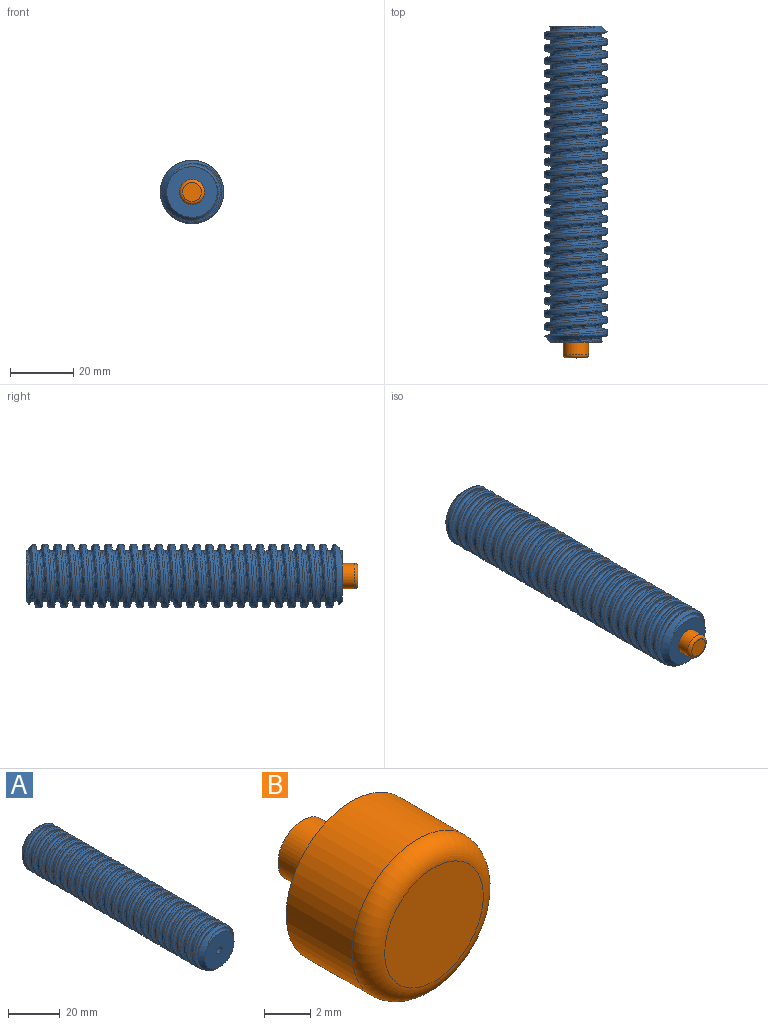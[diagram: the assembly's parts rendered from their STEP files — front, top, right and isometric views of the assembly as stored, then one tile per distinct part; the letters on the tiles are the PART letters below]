
ASSEMBLY  parts=2 mates=1
PART A: 13 faces, bbox 20x102.1x23.1 mm
  f0: cylinder r=10mm len=96mm, axis (0,1,0), area 2402.1mm2, adj f3,f4,f11,f12
  f1: plane 16x16mm, normal (0,-1,0), area 194mm2, adj f4,f7
  f2: plane 16x16mm, normal (0,1,0), area 201.1mm2, adj f3,f9
  f3: cone r=10mm half-angle=45deg, axis (0,-1,0), area 91.7mm2, adj f0,f2,f5,f6,f9,f10,f11,f12
  f4: cone r=8mm half-angle=45deg, axis (0,1,0), area 91.7mm2, adj f0,f1,f5,f6,f9,f10,f11,f12
  f5: bspline ~98.67x23.09mm, area 709.7mm2, adj f3,f4,f9,f12
  f6: bspline ~98.67x23.09mm, area 711.5mm2, adj f3,f4,f10,f11
  f7: cylinder r=1.5mm len=3mm, axis (0,-1,0), area 28.3mm2, adj f1,f8
  f8: plane 3x3mm, normal (0,-1,0), area 7.1mm2, adj f7
  f9: bspline ~101.92x18.29mm, area 2113.3mm2, adj f2,f3,f4,f5,f10
  f10: bspline ~101.92x18.29mm, area 2120.6mm2, adj f3,f4,f6,f9
  f11: bspline ~97.65x20.03mm, area 1131.4mm2, adj f0,f3,f4,f6
  f12: bspline ~97.62x20.01mm, area 1131.4mm2, adj f0,f3,f4,f5
PART B: 6 faces, bbox 8.7x8x8.7 mm
  f0: cylinder r=1.5mm len=3mm, axis (0,-1,0), area 28.3mm2, adj f1,f4
  f1: plane 3x3mm, normal (0,1,0), area 7.1mm2, adj f0
  f2: cylinder r=4mm len=8mm, axis (0,1,0), area 100.5mm2, adj f4,f5
  f3: plane 6x6mm, normal (0,-1,0), area 28.3mm2, adj f5
  f4: plane 8x8mm, normal (0,1,0), area 43.2mm2, adj f0,f2
  f5: torus R=3mm, axis (0,-1,0), area 35.9mm2, adj f2,f3
PLACE A t=(-5.42,-1.81,1.97)mm
PLACE B t=(-5.42,-1.81,1.97)mm
MATE fastened B.f0 <-> A.f7  axis (0,1,0) through (-5.42,-51.81,1.97)mm
